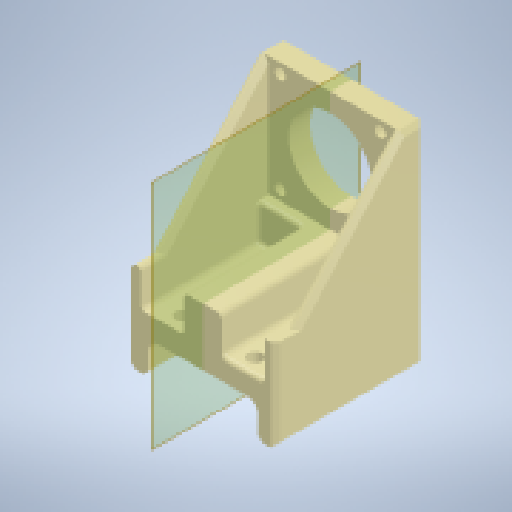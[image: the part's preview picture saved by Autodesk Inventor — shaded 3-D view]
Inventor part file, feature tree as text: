
AUTODESK INVENTOR PART (.ipt)
format: ipt  version: 2023 (Build 270158000, 158)  size: 443,392 bytes
history: native  units: mm
features: extrude x7, sketch x6, fillet x2, projected_geometry x2, plane x1, mirror x1, chamfer x1
ambient origin geometry x8: Origin, YZ Plane, XZ Plane, XY Plane, X Axis, Y Axis, Z Axis, Center Point
bodies: Solid1 (feature_tree)
feature tree (20):
  extrude  "Extrusion1"  Depth=5.0mm
  extrude  "Extrusion2"  Depth=10.0mm TaperAngle=0.0deg
  plane  "Work Plane2"
  mirror  "Mirror2"
  extrude  "Extrusion6"  Depth=5.0mm TaperAngle=0.0deg
  extrude  "Extrusion7"  Depth=15.0mm TaperAngle=0.0deg
  fillet  "Fillet1"  Radius=17.5mm
  extrude  "Extrusion8"  Depth=10.0mm TaperAngle=0.0deg
  extrude  "Extrusion9"  Depth=56.4mm
  chamfer  "Chamfer3"  Distance=35.0mm
  extrude  "Extrusion10"  Depth=56.4mm
  fillet  "Fillet2"  Radius=44.75mm
  sketch  "Sketch2"  dims[d0=47.14mm d1=5.0mm d2=58.0mm]
  projected_geometry  "Projected Loop3"
  sketch  "Sketch7"  dims[d4=39.0mm d5=10.0mm d6=0.0mm]
  sketch  "Sketch8"  dims[d7=50.0mm d8=5.0mm d9=0.0mm]
  sketch  "Sketch9"  dims[d34=55.4mm d35=15.0mm d36=0.0mm d37=17.5mm]
  projected_geometry  "Projected Loop4"
  sketch  "Sketch10"  dims[d38=10.0mm d39=55.0mm d40=0.0mm]
  sketch  "Sketch11"  dims[d41=2.0mm d45=6.7625mm d46=35.0mm d47=34.0mm d49=44.75mm d50=0.0mm d51=51.8mm d52=5.08mm d53=15.5mm d54=2.0mm d55=0.0mm d56=2.0mm d57=2.0mm d58=45.0deg d59=25.0mm d60=22.5mm d61=10.0mm d62=0.0mm d63=2.0mm d64=56.4mm d65=7.5mm]
